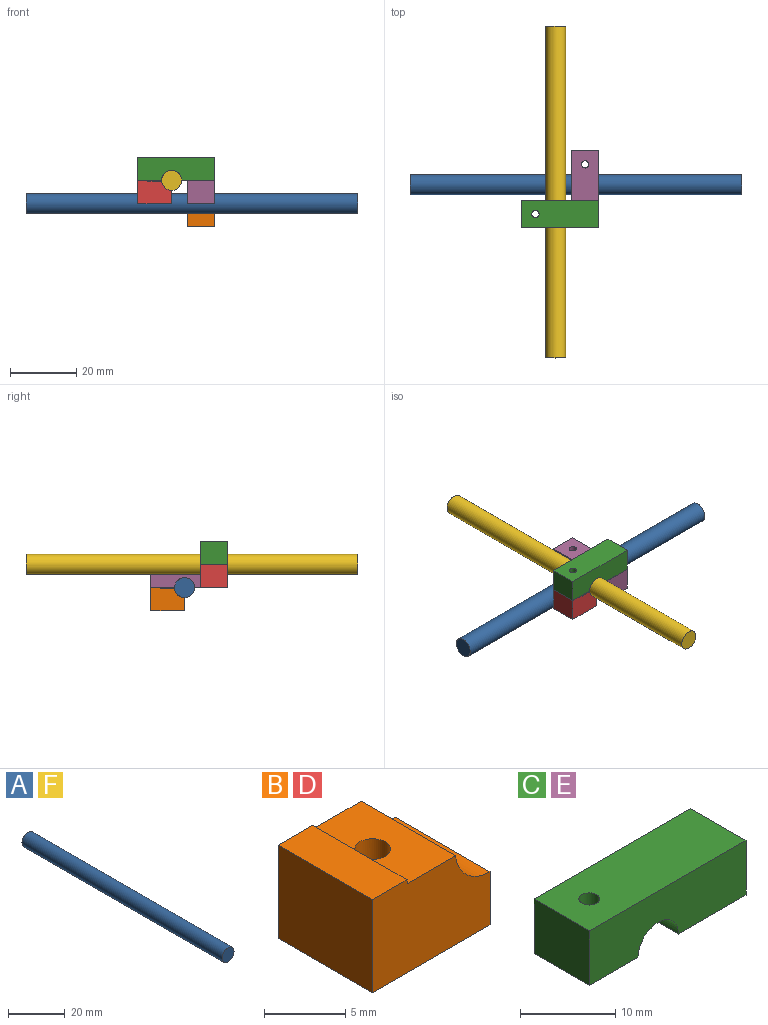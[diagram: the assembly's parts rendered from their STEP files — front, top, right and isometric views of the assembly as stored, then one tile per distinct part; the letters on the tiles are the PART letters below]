
ASSEMBLY  parts=6 mates=11
PART A: 3 faces, bbox 6x100x6 mm
  f0: cylinder r=3mm len=100mm, axis (0,1,0), area 1885mm2, adj f1,f2
  f1: plane 6x6mm, normal (0,-1,0), area 28.3mm2, adj f0
  f2: plane 6x6mm, normal (0,1,0), area 28.3mm2, adj f0
PART B: 10 faces, bbox 10.2x8.2x7 mm
  f0: plane 8.2x3mm, normal (0,0,1), area 24.6mm2, adj f1,f6,f7,f8
  f1: plane 8.2x7mm, normal (-1,0,0), area 57.4mm2, adj f0,f2,f7,f8
  f2: plane 10.2x8.2mm, normal (0,0,-1), area 79.8mm2, adj f1,f3,f7,f8,f9
  f3: plane 8.2x4mm, normal (1,0,0), area 32.8mm2, adj f2,f4,f7,f8
  f4: cylinder r=3mm len=8.2mm, axis (0,1,0), area 36.2mm2, adj f3,f5,f7,f8
  f5: plane 8.2x4.22mm, normal (0,0,1), area 30.8mm2, adj f4,f6,f7,f8,f9
  f6: plane 8.2x0.3mm, normal (1,0,0), area 2.5mm2, adj f0,f5,f7,f8
  f7: plane 10.2x7mm, normal (0,-1,0), area 63.1mm2, adj f0,f1,f2,f3,f4,f5,f6
  f8: plane 10.2x7mm, normal (0,1,0), area 63.1mm2, adj f0,f1,f2,f3,f4,f5,f6
  f9: cylinder r=1.1mm len=6.7mm, axis (0,0,-1), area 46.3mm2, adj f2,f5
PART C: 9 faces, bbox 23.2x8.2x7 mm
  f0: plane 8.2x7mm, normal (-1,0,0), area 57.4mm2, adj f1,f5,f6,f7
  f1: plane 8.2x7.2mm, normal (0,0,-1), area 55.2mm2, adj f0,f2,f6,f7,f8
  f2: cylinder r=3mm len=8.2mm, axis (0,1,0), area 77.3mm2, adj f1,f3,f6,f7
  f3: plane 10x8.2mm, normal (0,0,-1), area 82mm2, adj f2,f4,f6,f7
  f4: plane 8.2x7mm, normal (1,0,0), area 57.4mm2, adj f3,f5,f6,f7
  f5: plane 23.2x8.2mm, normal (0,0,1), area 186.4mm2, adj f0,f4,f6,f7,f8
  f6: plane 23.2x7mm, normal (0,-1,0), area 148.3mm2, adj f0,f1,f2,f3,f4,f5
  f7: plane 23.2x7mm, normal (0,1,0), area 148.3mm2, adj f0,f1,f2,f3,f4,f5
  f8: cylinder r=1.1mm len=7mm, axis (0,0,1), area 48.4mm2, adj f1,f5
PART D: same geometry as B
PART E: same geometry as C
PART F: same geometry as A
PLACE A rot(axis=(0.58,0.58,-0.58),120deg) t=(-1.05,2.45,25.43)mm
PLACE B rot(axis=(0,0,-1),90deg) t=(1.72,-44.64,-11.09)mm
PLACE C t=(-7.18,-6.45,-4.09)mm
PLACE D t=(39.9,-6.45,-4.09)mm
PLACE E rot(axis=(0,0,-1),90deg) t=(1.72,2.45,-11.09)mm
PLACE F t=(-43.7,0.22,-4.09)mm
MATE planar B.f1 <-> E.f0  axis (0,1,0) through (1.72,12.65,-14.59)mm
MATE slider E.f2 <-> A.f0  axis (1,0,0) through (1.72,2.45,-11.09)mm
MATE planar E.f5 <-> C.f3  axis (0,0,1) through (1.72,0.89,-4.09)mm
MATE planar E.f4 <-> C.f6  axis (0,-1,0) through (1.72,-10.55,-7.59)mm
MATE planar D.f0 <-> C.f1  axis (0,0,1) through (-15.88,-2.35,-4.09)mm
MATE planar B.f8 <-> E.f7  axis (1,0,0) through (5.82,7.97,-14.9)mm
MATE planar D.f8 <-> C.f7  axis (0,1,0) through (-12.71,-2.35,-7.9)mm
MATE slider C.f2 <-> F.f0  axis (0,1,0) through (-7.18,-10.55,-4.09)mm
MATE planar B.f0 <-> E.f1  axis (0,0,1) through (1.72,11.15,-11.09)mm
MATE planar E.f7 <-> C.f4  axis (1,0,0) through (5.82,5.45,-11.09)mm
MATE planar D.f1 <-> C.f0  axis (-1,0,0) through (-17.38,-6.45,-7.59)mm
